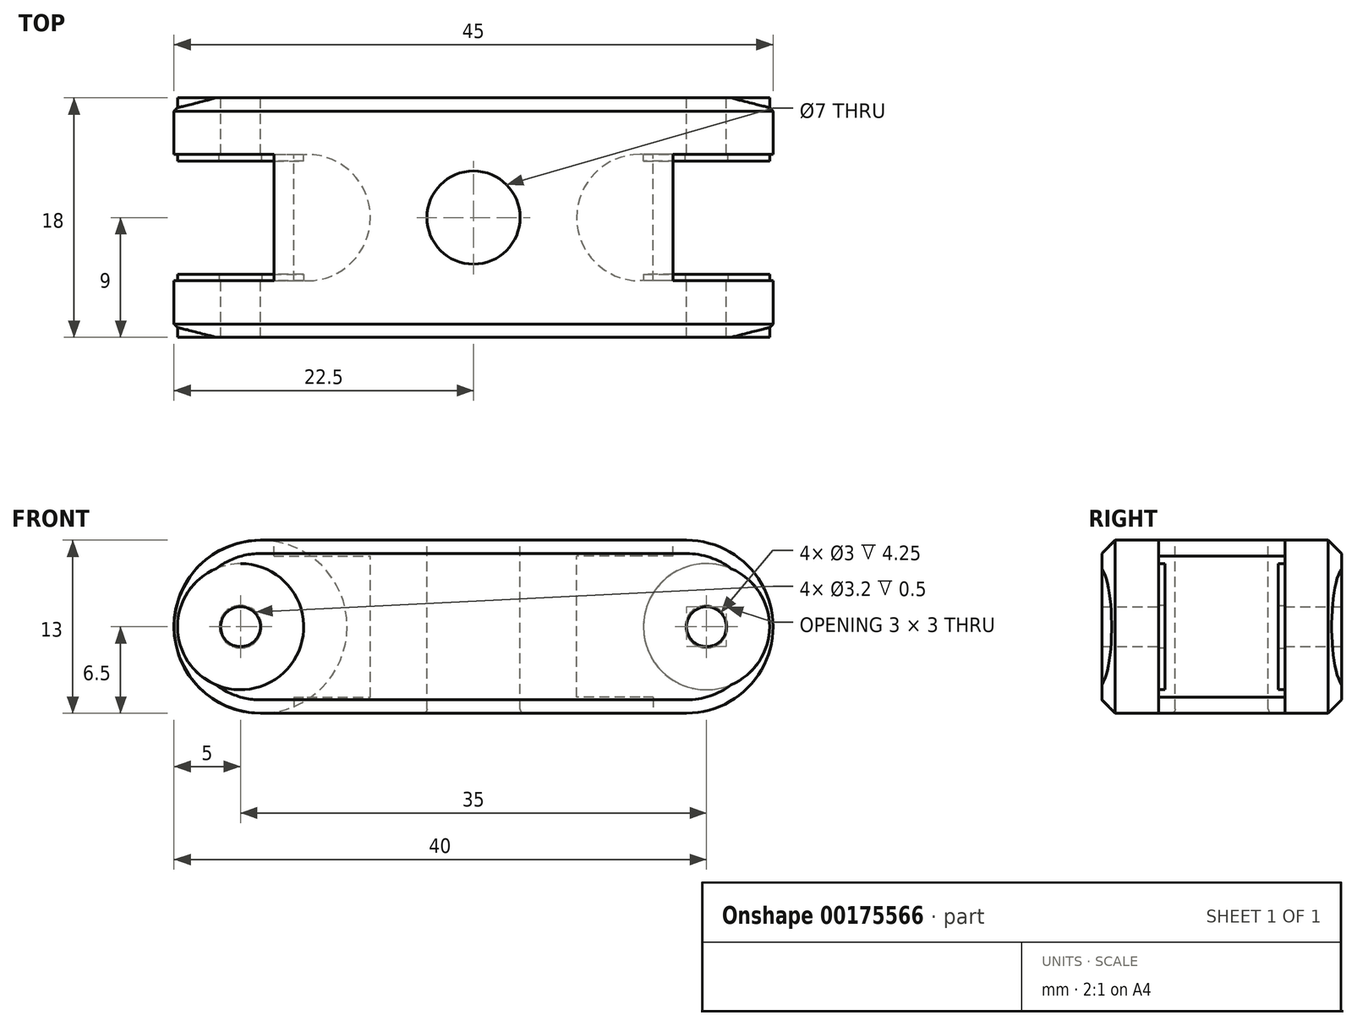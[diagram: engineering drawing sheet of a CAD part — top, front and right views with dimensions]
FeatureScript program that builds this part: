
annotation { "Feature Type Name" : "Feature", "Feature Type Description" : "" }
export const myFeature = defineFeature(function(context is Context, id is Id, definition is map)
    precondition{}
    {
        {
            var Q0;
            Q0=qCreatedBy(makeId("Front.planeOp"),FACE);
            var sketch = newSketch(context, id + "F0", { "sketchPlane" : qUnion([Q0])});
            skCircle(sketch, "E0", {"center": v(17.5, 0) * mm, "radius": 1.5 * mm});
            skCircle(sketch, "E1", {"center": v(-17.5, 0) * mm, "radius": 1.5 * mm});
            skArc(sketch, "E2", {"start": v(-16, 6.5) * mm, "mid": v(-22.5, 0) * mm, "end": v(-16, -6.5) * mm});
            skArc(sketch, "E3.MirrorCS", {"start": v(16, 6.5) * mm, "mid": v(22.5, 0) * mm, "end": v(16, -6.5) * mm});
            skLineSegment(sketch, "E4", {"start": v(-16, 6.5) * mm, "end": v(16, 6.5) * mm});
            skLineSegment(sketch, "E5.MirrorCS", {"start": v(-16, -6.5) * mm, "end": v(16, -6.5) * mm});
            skSolve(sketch);
        }
        {
            var Q0;
            Q0 = qSketchRegion(id + "F0", true);
            extrude(context, id + "F1", {"entities" : qUnion([Q0]), "depth" : 18 * mm});
        }
        {
            var Q0;
            Q0=makeQuery(id+"F1.opExtrude","SWEPT_FACE",FACE,{"disambiguationData":[OSD([sQuery(id+"F0.wireOp",EDGE,"E4")])]});
            var sketch = newSketch(context, id + "F2", { "sketchPlane" : qUnion([Q0])});
            skCircle(sketch, "E6", {"center": v(0, -9) * mm, "radius": 3.5 * mm});
            skSolve(sketch);
        }
        {
            var Q0;
            Q0 = qSketchRegion(id + "F2", true);
            extrude(context, id + "F3", {"entities" : qUnion([Q0]), "operationType" : NewBodyOperationType.REMOVE, "endBound" : BoundingType.THROUGH_ALL, "oppositeDirection" : true, "depth" : 25 * mm});
        }
        {
            var Q0;
            Q0=makeQuery(id+"F1.opExtrude","SWEPT_FACE",FACE,{"disambiguationData":[OSD([sQuery(id+"F0.wireOp",EDGE,"E4")])]});
            var sketch = newSketch(context, id + "F4", { "sketchPlane" : qUnion([Q0])});
            skLineSegment(sketch, "E7.bottom", {"start": v(-23.5, -4.25) * mm, "end": v(-12.5, -4.25) * mm});
            skLineSegment(sketch, "E7.top", {"start": v(-23.5, -13.75) * mm, "end": v(-12.5, -13.75) * mm});
            skLineSegment(sketch, "E7.left", {"start": v(-23.5, -4.25) * mm, "end": v(-23.5, -13.75) * mm});
            skArc(sketch, "E8", {"start": v(-12.5, -13.75) * mm, "mid": v(-7.75, -9) * mm, "end": v(-12.5, -4.25) * mm});
            skArc(sketch, "E9.MirrorCS", {"start": v(12.5, -13.75) * mm, "mid": v(7.75, -9) * mm, "end": v(12.5, -4.25) * mm});
            skLineSegment(sketch, "E10.MirrorCS", {"start": v(23.5, -13.75) * mm, "end": v(12.5, -13.75) * mm});
            skLineSegment(sketch, "E11.MirrorCS", {"start": v(23.5, -4.25) * mm, "end": v(23.5, -13.75) * mm});
            skLineSegment(sketch, "E12.MirrorCS", {"start": v(23.5, -4.25) * mm, "end": v(12.5, -4.25) * mm});
            skSolve(sketch);
        }
        {
            var Q0;
            Q0 = qSketchRegion(id + "F4", true);
            extrude(context, id + "F5", {"entities" : qUnion([Q0]), "operationType" : NewBodyOperationType.REMOVE, "endBound" : BoundingType.THROUGH_ALL, "oppositeDirection" : true, "depth" : 25 * mm});
        }
        {
            var Q0;
            Q0=makeQuery(id+"F1.opExtrude","SWEPT_FACE",FACE,{"disambiguationData":[OSD([sQuery(id+"F0.wireOp",EDGE,"E4")])]});
            var sketch = newSketch(context, id + "F6", { "sketchPlane" : qUnion([Q0])});
            skLineSegment(sketch, "E13.bottom", {"start": v(-15, -4.25) * mm, "end": v(-12.5, -4.25) * mm});
            skLineSegment(sketch, "E13.top", {"start": v(-15, -13.75) * mm, "end": v(-12.5, -13.75) * mm});
            skLineSegment(sketch, "E13.left", {"start": v(-15, -4.25) * mm, "end": v(-15, -13.75) * mm});
            skArc(sketch, "E14", {"start": v(-12.5, -13.75) * mm, "mid": v(-7.75, -9) * mm, "end": v(-12.5, -4.25) * mm});
            skArc(sketch, "E15.MirrorCS", {"start": v(12.5, -13.75) * mm, "mid": v(7.75, -9) * mm, "end": v(12.5, -4.25) * mm});
            skLineSegment(sketch, "E16.MirrorCS", {"start": v(15, -4.25) * mm, "end": v(12.5, -4.25) * mm});
            skLineSegment(sketch, "E17.MirrorCS", {"start": v(15, -4.25) * mm, "end": v(15, -13.75) * mm});
            skLineSegment(sketch, "E18.MirrorCS", {"start": v(15, -13.75) * mm, "end": v(12.5, -13.75) * mm});
            skSolve(sketch);
        }
        {
            var Q0;
            Q0 = qSketchRegion(id + "F6", true);
            extrude(context, id + "F7", {"entities" : qUnion([Q0]), "operationType" : NewBodyOperationType.ADD, "oppositeDirection" : true, "depth" : 1.2 * mm});
        }
        {
            var Q0;
            Q0=makeQuery(id+"F1.opExtrude","SWEPT_FACE",FACE,{"disambiguationData":[OSD([sQuery(id+"F0.wireOp",EDGE,"E5.MirrorCS")])]});
            var sketch = newSketch(context, id + "F8", { "sketchPlane" : qUnion([Q0])});
            skLineSegment(sketch, "E19.bottom", {"start": v(-13.5, 13.75) * mm, "end": v(-12.5, 13.75) * mm});
            skLineSegment(sketch, "E19.top", {"start": v(-13.5, 4.25) * mm, "end": v(-12.5, 4.25) * mm});
            skLineSegment(sketch, "E19.left", {"start": v(-13.5, 13.75) * mm, "end": v(-13.5, 4.25) * mm});
            skArc(sketch, "E20", {"start": v(-12.5, 4.25) * mm, "mid": v(-7.75, 9) * mm, "end": v(-12.5, 13.75) * mm});
            skArc(sketch, "E21.MirrorCS", {"start": v(12.5, 4.25) * mm, "mid": v(7.75, 9) * mm, "end": v(12.5, 13.75) * mm});
            skLineSegment(sketch, "E22.MirrorCS", {"start": v(13.5, 13.75) * mm, "end": v(13.5, 4.25) * mm});
            skLineSegment(sketch, "E23.MirrorCS", {"start": v(13.5, 13.75) * mm, "end": v(12.5, 13.75) * mm});
            skLineSegment(sketch, "E24.MirrorCS", {"start": v(13.5, 4.25) * mm, "end": v(12.5, 4.25) * mm});
            skSolve(sketch);
        }
        {
            var Q0;
            Q0 = qSketchRegion(id + "F8", true);
            extrude(context, id + "F9", {"entities" : qUnion([Q0]), "operationType" : NewBodyOperationType.ADD, "oppositeDirection" : true, "depth" : 1.2 * mm});
        }
        {
            var Q0;
            Q0=makeQuery(id+"F7.opExtrude","SWEPT_EDGE",EDGE,{"disambiguationData":[OSD([sQuery(id+"F4.wireOp",EDGE,"E7.bottom"),sQuery(id+"F6.wireOp",EDGE,"E13.bottom"),sQuery(id+"F6.wireOp",EDGE,"E13.left")])]});
            var Q1;
            Q1=makeQuery(id+"F9.opExtrude","SWEPT_EDGE",EDGE,{"disambiguationData":[OSD([sQuery(id+"F0.wireOp",EDGE,"E5.MirrorCS"),sQuery(id+"F4.wireOp",EDGE,"E7.bottom"),sQuery(id+"F8.wireOp",EDGE,"E19.top"),sQuery(id+"F8.wireOp",EDGE,"E19.left")])]});
            var Q2;
            Q2=makeQuery(id+"F7.opExtrude","CAP_EDGE",EDGE,{"disambiguationData":[OSD([sQuery(id+"F6.wireOp",EDGE,"E13.bottom")])],"isStart":false});
            var Q3;
            Q3=makeQuery(id+"F7.opExtrude","SWEPT_EDGE",EDGE,{"disambiguationData":[OSD([sQuery(id+"F4.wireOp",EDGE,"E7.top"),sQuery(id+"F6.wireOp",EDGE,"E13.top"),sQuery(id+"F6.wireOp",EDGE,"E13.left")])]});
            var Q4;
            Q4=makeQuery(id+"F9.opExtrude","SWEPT_EDGE",EDGE,{"disambiguationData":[OSD([sQuery(id+"F0.wireOp",EDGE,"E5.MirrorCS"),sQuery(id+"F4.wireOp",EDGE,"E7.top"),sQuery(id+"F8.wireOp",EDGE,"E19.bottom"),sQuery(id+"F8.wireOp",EDGE,"E19.left")])]});
            var Q5;
            Q5=makeQuery(id+"F9.opExtrude","CAP_EDGE",EDGE,{"disambiguationData":[OSD([sQuery(id+"F8.wireOp",EDGE,"E19.bottom")])],"isStart":false});
            var Q6;
            Q6=makeQuery(id+"F7.opExtrude","SWEPT_EDGE",EDGE,{"disambiguationData":[OSD([sQuery(id+"F4.wireOp",EDGE,"E10.MirrorCS"),sQuery(id+"F6.wireOp",EDGE,"E17.MirrorCS"),sQuery(id+"F6.wireOp",EDGE,"E18.MirrorCS")])]});
            var Q7;
            Q7=makeQuery(id+"F7.opExtrude","CAP_EDGE",EDGE,{"disambiguationData":[OSD([sQuery(id+"F6.wireOp",EDGE,"E18.MirrorCS")])],"isStart":false});
            var Q8;
            Q8=makeQuery(id+"F9.opExtrude","SWEPT_EDGE",EDGE,{"disambiguationData":[OSD([sQuery(id+"F0.wireOp",EDGE,"E5.MirrorCS"),sQuery(id+"F4.wireOp",EDGE,"E10.MirrorCS"),sQuery(id+"F8.wireOp",EDGE,"E22.MirrorCS"),sQuery(id+"F8.wireOp",EDGE,"E23.MirrorCS")])]});
            var Q9;
            Q9=makeQuery(id+"F7.opExtrude","SWEPT_EDGE",EDGE,{"disambiguationData":[OSD([sQuery(id+"F4.wireOp",EDGE,"E12.MirrorCS"),sQuery(id+"F6.wireOp",EDGE,"E16.MirrorCS"),sQuery(id+"F6.wireOp",EDGE,"E17.MirrorCS")])]});
            var Q10;
            Q10=makeQuery(id+"F9.opExtrude","SWEPT_EDGE",EDGE,{"disambiguationData":[OSD([sQuery(id+"F0.wireOp",EDGE,"E5.MirrorCS"),sQuery(id+"F4.wireOp",EDGE,"E12.MirrorCS"),sQuery(id+"F8.wireOp",EDGE,"E22.MirrorCS"),sQuery(id+"F8.wireOp",EDGE,"E24.MirrorCS")])]});
            var Q11;
            Q11=makeQuery(id+"F9.opExtrude","CAP_EDGE",EDGE,{"disambiguationData":[OSD([sQuery(id+"F8.wireOp",EDGE,"E24.MirrorCS")])],"isStart":false});
            var Q12;
            Q12=makeQuery(id+"F3.boolean.opBoolean","COPY",EDGE,{"derivedFrom":makeQuery(id+"F3.opExtrude","CAP_EDGE",EDGE,{"disambiguationData":[OSD([sQuery(id+"F2.wireOp",EDGE,"E6")])],"isStart":true})});
            var Q13;
            Q13=makeQuery(id+"F3.boolean.opBoolean","INTERSECT",EDGE,{"derivedFrom":[makeQuery(id+"F1.opExtrude","SWEPT_FACE",FACE,{"disambiguationData":[OSD([sQuery(id+"F0.wireOp",EDGE,"E5.MirrorCS")])]}),makeQuery(id+"F3.opExtrude","SWEPT_FACE",FACE,{"disambiguationData":[OSD([sQuery(id+"F2.wireOp",EDGE,"E6")])]})]});
            fillet(context, id + "F10", {"entities" : qUnion([Q0, Q1, Q2, Q3, Q4, Q5, Q6, Q7, Q8, Q9, Q10, Q11, Q12, Q13]), "radius" : .3 * mm, "tangentPropagation" : true, "allowEdgeOverflow" : false});
        }
        {
            var Q0;
            Q0=makeQuery(id+"F1.opExtrude","CAP_EDGE",EDGE,{"disambiguationData":[OSD([sQuery(id+"F0.wireOp",EDGE,"E4")])],"isStart":false});
            var Q1;
            Q1=makeQuery(id+"F1.opExtrude","CAP_EDGE",EDGE,{"disambiguationData":[OSD([sQuery(id+"F0.wireOp",EDGE,"E5.MirrorCS")])],"isStart":true});
            chamfer(context, id + "F11", {"entities" : qUnion([Q0, Q1]), "width" : 1 * mm, "tangentPropagation" : true});
        }
        {
            var Q0;
            Q0=makeQuery(id+"F1.opExtrude","CAP_FACE",FACE,{"disambiguationData":[OSD([sQuery(id+"F0.wireOp",EDGE,"E0"),sQuery(id+"F0.wireOp",EDGE,"E1"),sQuery(id+"F0.wireOp",EDGE,"E2"),sQuery(id+"F0.wireOp",EDGE,"E3.MirrorCS"),sQuery(id+"F0.wireOp",EDGE,"E4"),sQuery(id+"F0.wireOp",EDGE,"E5.MirrorCS")])],"isStart":false});
            var sketch = newSketch(context, id + "F12", { "sketchPlane" : qUnion([Q0])});
            skCircle(sketch, "E25", {"center": v(-17.5, 0) * mm, "radius": 4.74 * mm});
            skCircle(sketch, "E26.MirrorC", {"center": v(17.5, 0) * mm, "radius": 4.74 * mm});
            skCircle(sketch, "E27", {"center": v(-17.5, 0) * mm, "radius": 1.6 * mm});
            skCircle(sketch, "E28.MirrorC", {"center": v(17.5, 0) * mm, "radius": 1.6 * mm});
            skSolve(sketch);
        }
        {
            var Q0;
            Q0 = qSketchRegion(id + "F12", true);
            extrude(context, id + "F13", {"entities" : qUnion([Q0]), "operationType" : NewBodyOperationType.ADD, "oppositeDirection" : true, "depth" : 4.75 * mm});
        }
        {
            var Q0;
            Q0=makeQuery(id+"F1.opExtrude","CAP_FACE",FACE,{"disambiguationData":[OSD([sQuery(id+"F0.wireOp",EDGE,"E0"),sQuery(id+"F0.wireOp",EDGE,"E1"),sQuery(id+"F0.wireOp",EDGE,"E2"),sQuery(id+"F0.wireOp",EDGE,"E3.MirrorCS"),sQuery(id+"F0.wireOp",EDGE,"E4"),sQuery(id+"F0.wireOp",EDGE,"E5.MirrorCS")])],"isStart":true});
            var sketch = newSketch(context, id + "F14", { "sketchPlane" : qUnion([Q0])});
            skCircle(sketch, "E29", {"center": v(17.5, 0) * mm, "radius": 4.74 * mm});
            skCircle(sketch, "E30", {"center": v(17.5, 0) * mm, "radius": 1.6 * mm});
            skCircle(sketch, "E31.MirrorC", {"center": v(-17.5, 0) * mm, "radius": 1.6 * mm});
            skCircle(sketch, "E32.MirrorC", {"center": v(-17.5, 0) * mm, "radius": 4.74 * mm});
            skSolve(sketch);
        }
        {
            var Q0;
            Q0 = qSketchRegion(id + "F14", true);
            extrude(context, id + "F15", {"entities" : qUnion([Q0]), "operationType" : NewBodyOperationType.ADD, "oppositeDirection" : true, "depth" : 4.75 * mm});
        }
    });
